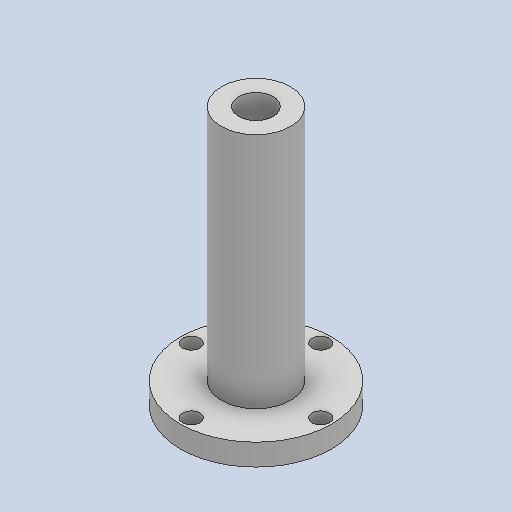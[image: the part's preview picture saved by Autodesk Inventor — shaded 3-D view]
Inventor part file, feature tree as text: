
AUTODESK INVENTOR PART (.ipt)
format: ipt  version: 2023 (Build 270158000, 158)  size: 128,000 bytes
history: native  units: mm
features: extrude x3, sketch x3
ambient origin geometry x8: Origin, YZ Plane, XZ Plane, XY Plane, X Axis, Y Axis, Z Axis, Center Point
bodies: Solid1 (feature_tree)
feature tree (6):
  extrude  "Extrusion1"  Depth=8.0mm
  extrude  "Extrusion2"  Depth=5.0mm
  extrude  "Extrusion3"  Depth=55.0mm
  sketch  "Sketch3"  dims[d0=8.0mm d1=35.0mm]
  sketch  "Sketch4"  dims[d2=5.0mm d3=0.0mm d4=16.0mm]
  sketch  "Sketch5"  dims[d5=8.0mm d6=55.0mm d7=0.0mm d8=4.0mm d9=15.0mm d10=15.0mm d11=15.0mm d12=15.0mm d13=4.0mm d14=4.0mm d15=4.0mm d16=55.0mm d17=0.0mm]
